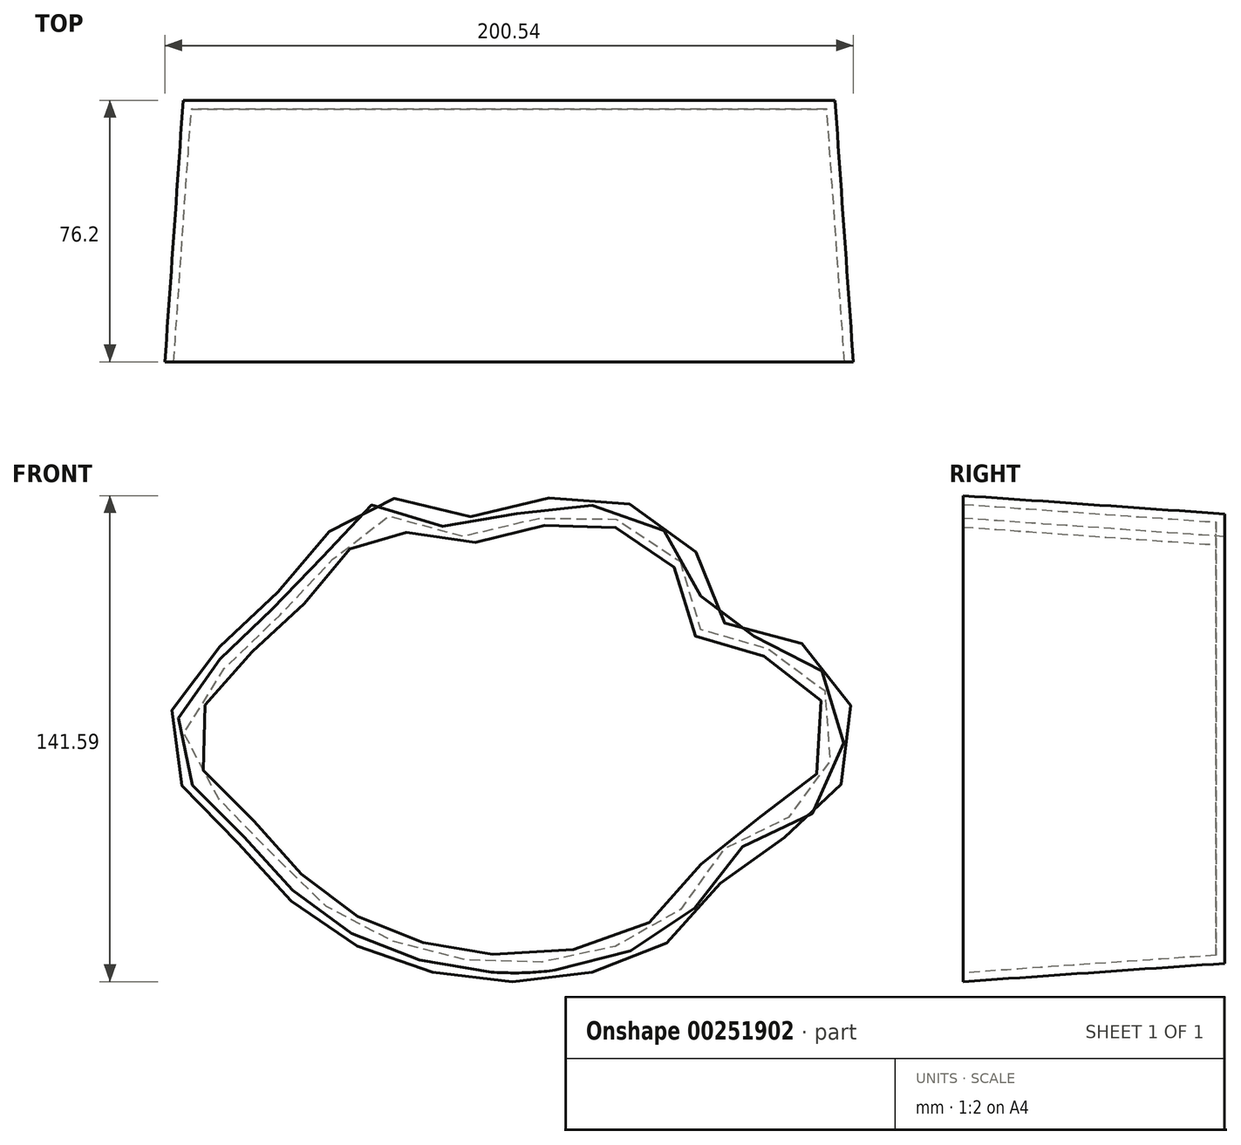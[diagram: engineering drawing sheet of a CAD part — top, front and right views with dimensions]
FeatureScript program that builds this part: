
annotation { "Feature Type Name" : "Feature", "Feature Type Description" : "" }
export const myFeature = defineFeature(function(context is Context, id is Id, definition is map)
    precondition{}
    {
        {
            var Q0;
            Q0=qCreatedBy(makeId("Front.planeOp"),FACE);
            var sketch = newSketch(context, id + "F0", { "sketchPlane" : qUnion([Q0])});
            skPoint(sketch, "E0.visualSharp", {"position": v(-72.18, 48.73) * mm});
            skPoint(sketch, "E1.visualSharp", {"position": v(80.22, 48.73) * mm});
            skPoint(sketch, "E2.visualSharp", {"position": v(80.22, -52.87) * mm});
            skPoint(sketch, "E3.visualSharp", {"position": v(-72.18, -52.87) * mm});
            skFitSpline(sketch, "E4", {"points": [v(-46.78, -52.87) * mm, v(-72.18, -27.47) * mm, v(-89.87, -4.75) * mm, v(-72.18, 23.33) * mm, v(-46.78, 48.73) * mm, v(-34.34, 62.47) * mm, v(-14.37, 56.14) * mm, v(21.92, 62.47) * mm, v(54.82, 48.73) * mm, v(61.38, 28.13) * mm, v(80.22, 23.33) * mm, v(99.62, 4.02) * mm, v(90.6, -23.5) * mm, v(80.22, -27.47) * mm, v(64.79, -38.12) * mm, v(54.82, -52.87) * mm, v(10.23, -68.32) * mm, v(-46.78, -52.87) * mm]});
            skSolve(sketch);
        }
        {
            var Q0;
            Q0=makeQuery(id+"F0.imprint","IMPRINT",FACE,{"disambiguationData":[TD([[makeQuery(id+"F0.imprint","IMPRINT",EDGE,{"derivedFrom":sQuery(id+"F0.wireOp",EDGE,"E4")}),-1.0]])]});
            extrude(context, id + "F1", {"entities" : qUnion([Q0]), "depth" : 76.2 * mm, "hasDraft" : true, "draftAngle" : 4 * degree});
        }
        {
            var Q0;
            Q0=makeQuery(id+"F1.opExtrude","CAP_FACE",FACE,{"disambiguationData":[OSD([sQuery(id+"F0.wireOp",EDGE,"E4")])],"isStart":false});
            shell(context, id + "F2", {"entities" : qUnion([Q0]), "thickness" : 2.54 * mm});
        }
    });
